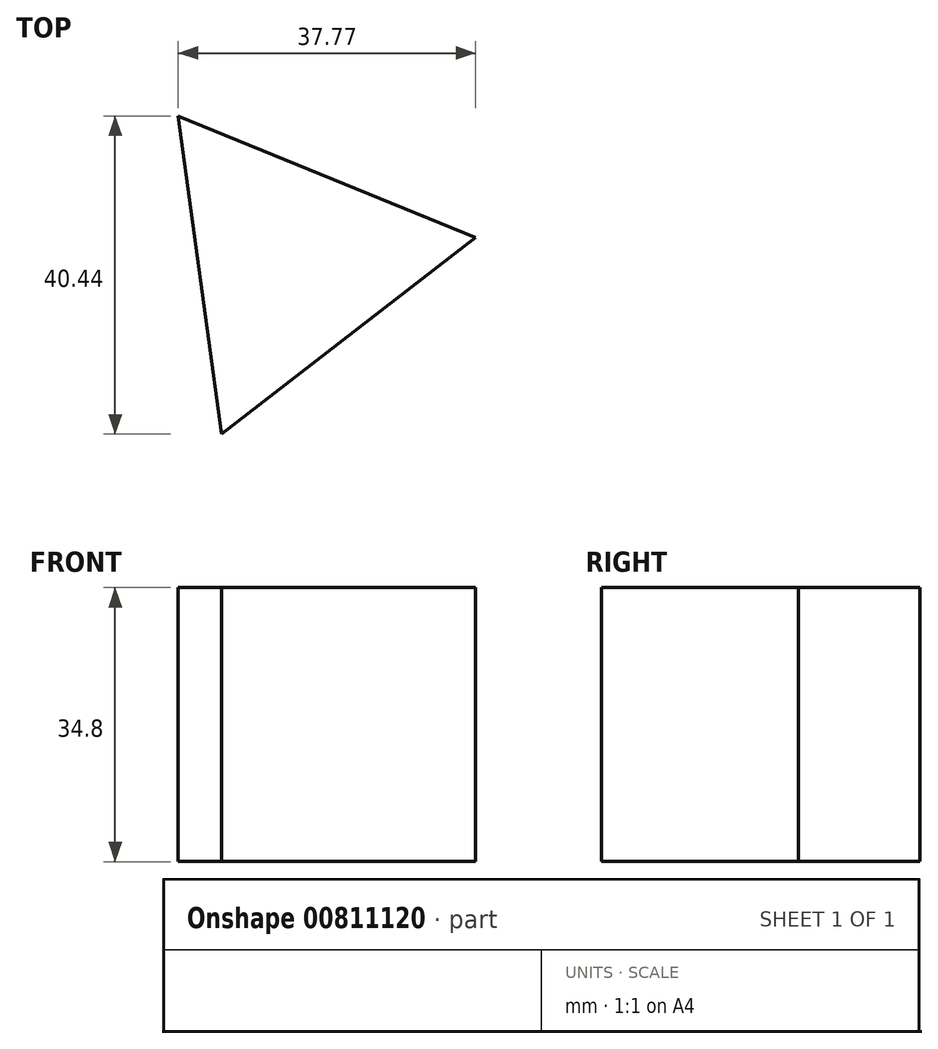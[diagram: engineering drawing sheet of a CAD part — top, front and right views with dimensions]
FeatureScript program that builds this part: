
annotation { "Feature Type Name" : "Feature", "Feature Type Description" : "" }
export const myFeature = defineFeature(function(context is Context, id is Id, definition is map)
    precondition{}
    {
        {
            var Q0;
            Q0=qCreatedBy(makeId("Top.planeOp"),FACE);
            var sketch = newSketch(context, id + "F0", { "sketchPlane" : qUnion([Q0])});
            skCircle(sketch, "E0.cCircle", {"center": v(0, 0) * mm, "radius": 11.78 * mm, "construction": true});
            skLineSegment(sketch, "E0.0", {"start": v(23.34, 3.18) * mm, "end": v(-8.92, -21.8) * mm});
            skLineSegment(sketch, "E0.1", {"start": v(-8.92, -21.8) * mm, "end": v(-14.43, 18.63) * mm});
            skLineSegment(sketch, "E0.2", {"start": v(-14.43, 18.63) * mm, "end": v(23.34, 3.18) * mm});
            skPoint(sketch, "E0.0.midPoint", {"position": v(7.21, -9.31) * mm});
            skSolve(sketch);
        }
        {
            var Q0;
            Q0=makeQuery(id+"F0.imprint","IMPRINT",FACE,{"disambiguationData":[TD([[makeQuery(id+"F0.imprint","IMPRINT",EDGE,{"derivedFrom":sQuery(id+"F0.wireOp",EDGE,"E0.0")}),-1.0]])]});
            extrude(context, id + "F1", {"entities" : qUnion([Q0]), "oppositeDirection" : true, "depth" : 34.8 * mm, "offsetDistance" : 25.4 * mm});
        }
    });
